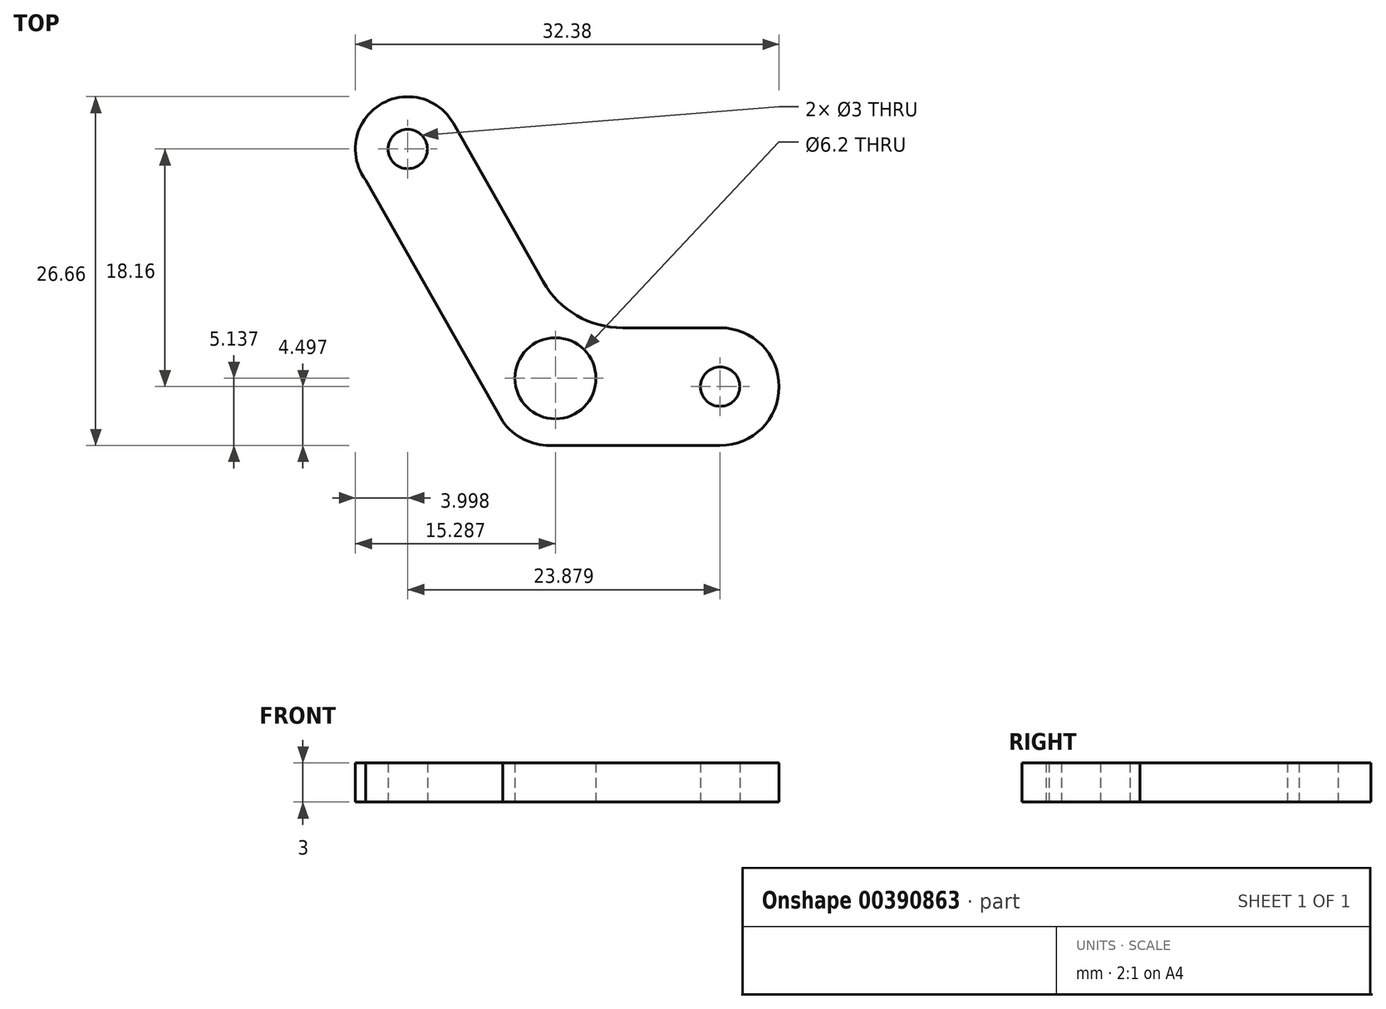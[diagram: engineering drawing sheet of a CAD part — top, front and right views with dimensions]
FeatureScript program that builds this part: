
annotation { "Feature Type Name" : "Feature", "Feature Type Description" : "" }
export const myFeature = defineFeature(function(context is Context, id is Id, definition is map)
    precondition{}
    {
        {
            var Q0;
            Q0=qCreatedBy(makeId("Top.planeOp"),FACE);
            var sketch = newSketch(context, id + "F0", { "sketchPlane" : qUnion([Q0])});
            skPoint(sketch, "E0.middle", {"position": v(0, 0) * mm});
            skPoint(sketch, "E1.third.point", {"position": v(-4.26, -1.84) * mm});
            skPoint(sketch, "E2.third.point", {"position": v(2.42, 0.68) * mm});
            skCircle(sketch, "E3", {"center": v(-10.17, 1.32) * mm, "radius": 3.1 * mm});
            skCircle(sketch, "E4", {"center": v(2.42, 0.68) * mm, "radius": 1.5 * mm});
            skLineSegment(sketch, "E5.bottom", {"start": v(-5.03, 5.18) * mm, "end": v(2.42, 5.18) * mm});
            skLineSegment(sketch, "E5.top", {"start": v(-10.58, -3.82) * mm, "end": v(2.42, -3.82) * mm});
            skArc(sketch, "E6", {"start": v(-14.2, -2) * mm, "mid": v(-12.61, -3.34) * mm, "end": v(-10.58, -3.82) * mm});
            skArc(sketch, "E7", {"start": v(2.42, -3.82) * mm, "mid": v(6.92, 0.68) * mm, "end": v(2.42, 5.18) * mm});
            skLineSegment(sketch, "E8", {"start": v(2.42, 0.68) * mm, "end": v(-21.46, 18.84) * mm, "construction": true});
            skLineSegment(sketch, "E9", {"start": v(2.42, 0.68) * mm, "end": v(-5.54, 6.73) * mm, "construction": true});
            skLineSegment(sketch, "E10", {"start": v(-5.54, 6.73) * mm, "end": v(0, 14.02) * mm, "construction": true});
            skCircle(sketch, "E11", {"center": v(-21.46, 18.84) * mm, "radius": 1.5 * mm});
            skArc(sketch, "E12", {"start": v(-17.98, 20.81) * mm, "mid": v(-23.64, 22.2) * mm, "end": v(-24.69, 16.47) * mm});
            skLineSegment(sketch, "E13", {"start": v(-25.15, 17.28) * mm, "end": v(-14.2, -2) * mm});
            skLineSegment(sketch, "E14", {"start": v(-17.98, 20.81) * mm, "end": v(-11.12, 8.72) * mm});
            skPoint(sketch, "E15.orphan", {"position": v(-10.58, 5.18) * mm});
            skPoint(sketch, "E16.visualSharp", {"position": v(-9.1, 5.18) * mm});
            skArc(sketch, "E16.filletArc", {"start": v(-11.12, 8.72) * mm, "mid": v(-8.55, 6.13) * mm, "end": v(-5.03, 5.18) * mm});
            skSolve(sketch);
        }
        {
            var Q0;
            Q0 = qSketchRegion(id + "F0", true);
            extrude(context, id + "F1", {"entities" : qUnion([Q0]), "depth" : 3 * mm, "offsetDistance" : 25 * mm});
        }
    });
